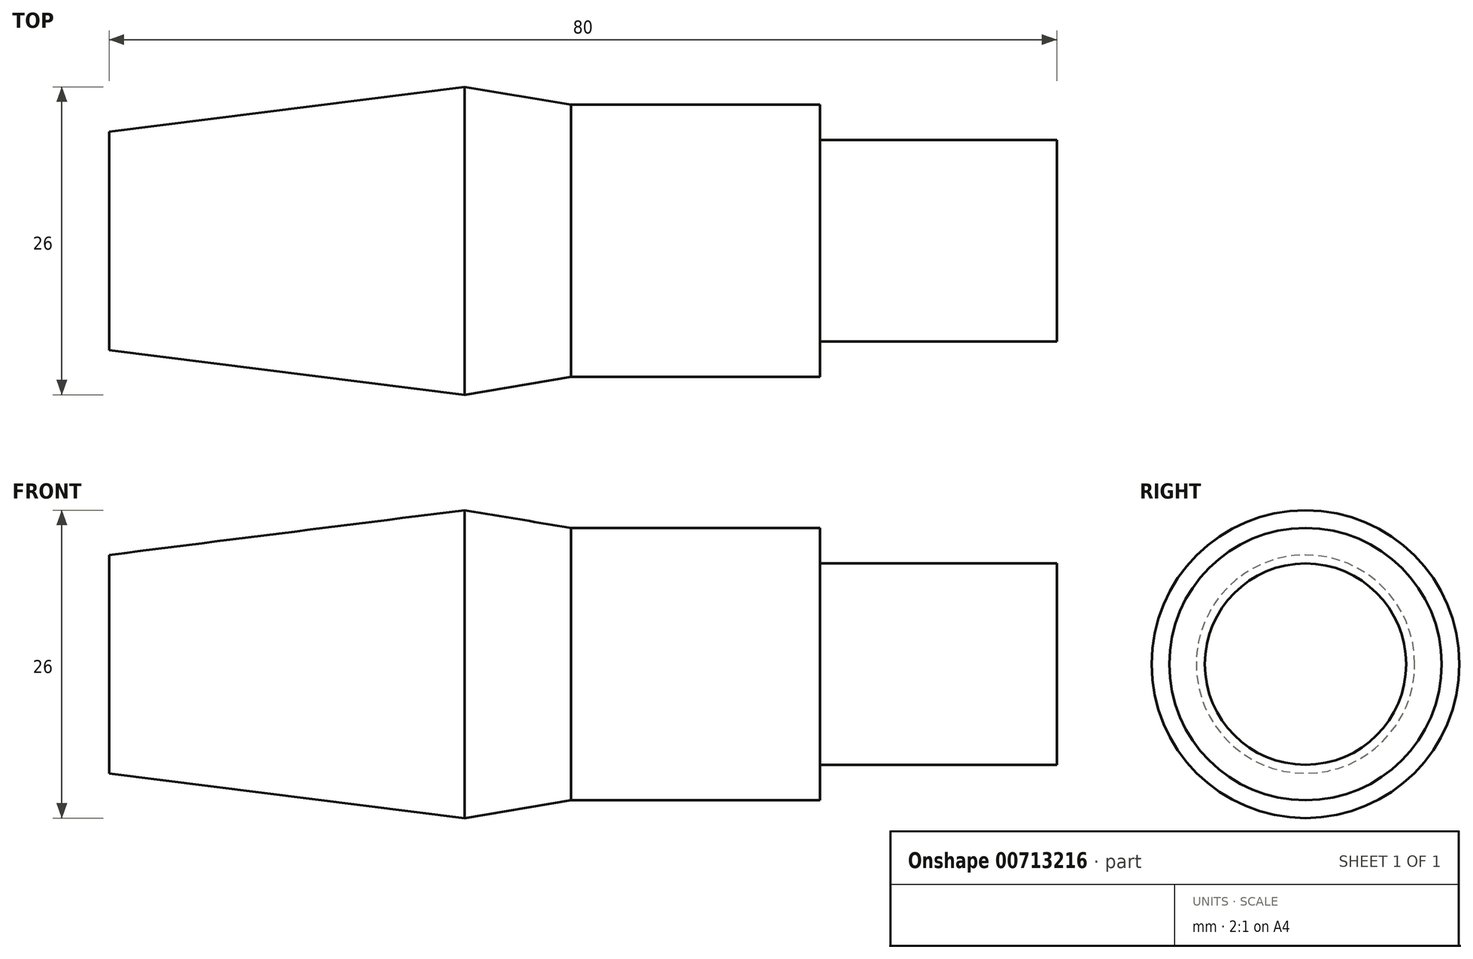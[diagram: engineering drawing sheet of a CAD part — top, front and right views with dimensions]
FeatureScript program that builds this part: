
annotation { "Feature Type Name" : "Feature", "Feature Type Description" : "" }
export const myFeature = defineFeature(function(context is Context, id is Id, definition is map)
    precondition{}
    {
        {
            var Q0;
            Q0=qCreatedBy(makeId("Front.planeOp"),FACE);
            var sketch = newSketch(context, id + "F0", { "sketchPlane" : qUnion([Q0])});
            skLineSegment(sketch, "E0", {"start": v(-34.88, 0) * mm, "end": v(-34.88, 9.22) * mm});
            skLineSegment(sketch, "E1", {"start": v(-34.88, 9.22) * mm, "end": v(-4.88, 13) * mm});
            skLineSegment(sketch, "E2", {"start": v(-4.88, 13) * mm, "end": v(4.12, 11.5) * mm});
            skLineSegment(sketch, "E3", {"start": v(4.12, 11.5) * mm, "end": v(25.12, 11.5) * mm});
            skLineSegment(sketch, "E4", {"start": v(25.12, 11.5) * mm, "end": v(25.12, 8.5) * mm});
            skLineSegment(sketch, "E5", {"start": v(25.12, 8.5) * mm, "end": v(45.12, 8.5) * mm});
            skLineSegment(sketch, "E6", {"start": v(45.12, 8.5) * mm, "end": v(45.12, 0) * mm});
            skLineSegment(sketch, "E7", {"start": v(45.12, 0) * mm, "end": v(-34.88, 0) * mm});
            skLineSegment(sketch, "E8", {"start": v(-51.16, 0) * mm, "end": v(50.53, 0) * mm, "construction": true});
            skSolve(sketch);
        }
        {
            var Q0;
            Q0=makeQuery(id+"F0.imprint","IMPRINT",FACE,{"disambiguationData":[TD([[makeQuery(id+"F0.imprint","IMPRINT",EDGE,{"derivedFrom":sQuery(id+"F0.wireOp",EDGE,"E0")}),-1.0]])]});
            var Q1;
            Q1=sQuery(id+"F0.wireOp",EDGE,"E8");
            revolve(context, id + "F1", {"surfaceOperationType" : NewSurfaceOperationType.NEW, "entities" : qUnion([Q0]), "axis" : qUnion([Q1]), "revolveType" : RevolveType.FULL});
        }
    });
